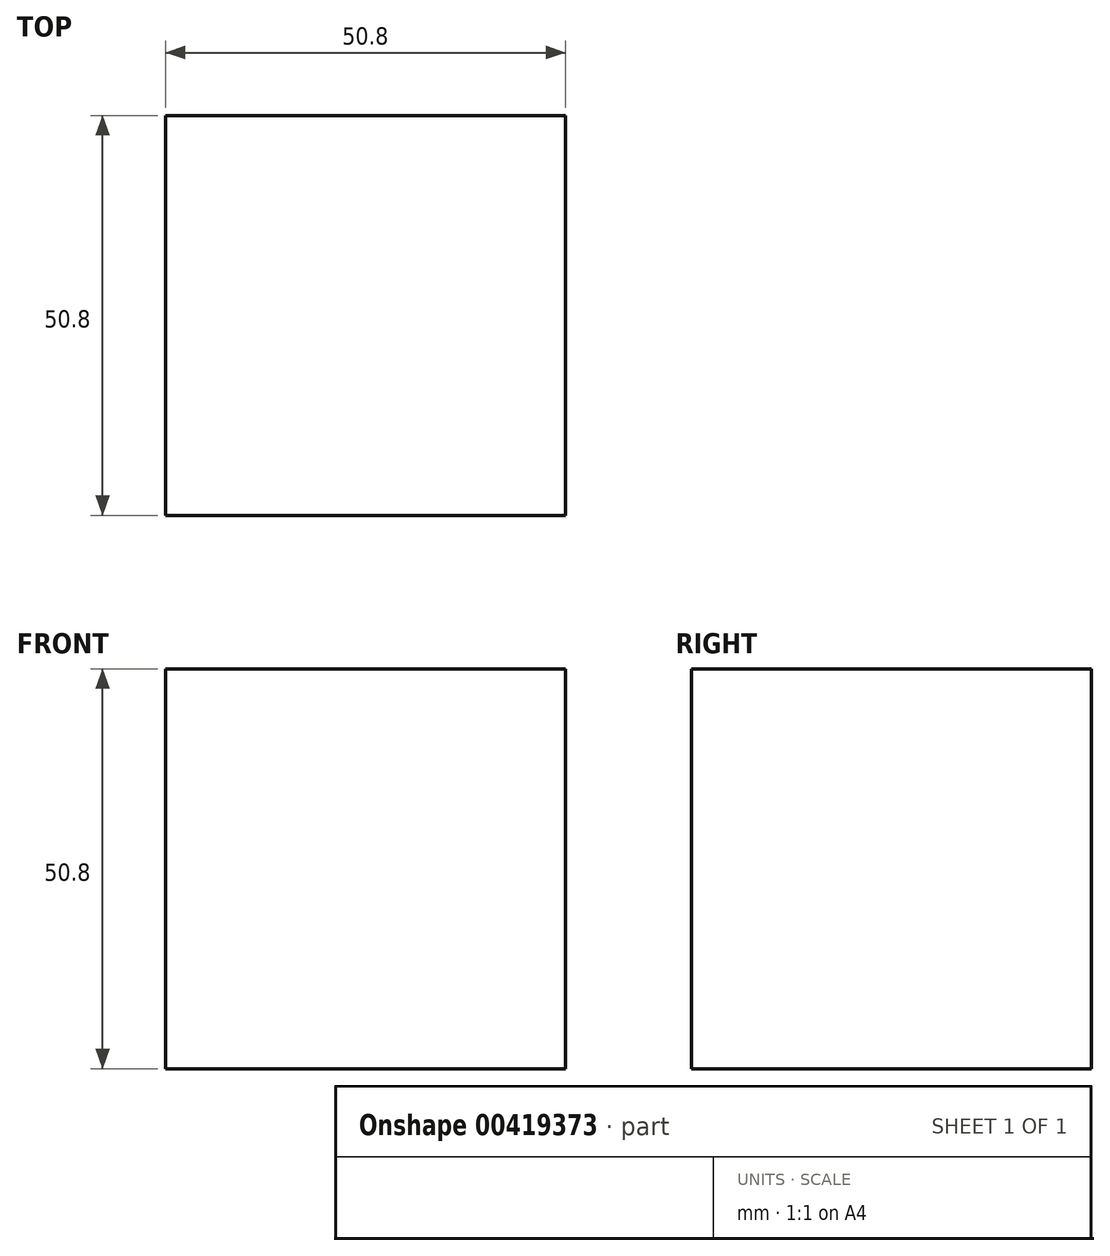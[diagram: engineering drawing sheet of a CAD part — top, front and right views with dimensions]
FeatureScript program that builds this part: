
annotation { "Feature Type Name" : "Feature", "Feature Type Description" : "" }
export const myFeature = defineFeature(function(context is Context, id is Id, definition is map)
    precondition{}
    {
        {
            var Q0;
            Q0=qCreatedBy(makeId("Front.planeOp"),FACE);
            var sketch = newSketch(context, id + "F0", { "sketchPlane" : qUnion([Q0])});
            skLineSegment(sketch, "E0", {"start": v(26.55, 20.82) * mm, "end": v(-24.25, 20.82) * mm});
            skLineSegment(sketch, "E1", {"start": v(-24.25, 20.82) * mm, "end": v(-24.25, -29.98) * mm});
            skLineSegment(sketch, "E2", {"start": v(-24.25, -29.98) * mm, "end": v(26.55, -29.98) * mm});
            skLineSegment(sketch, "E3", {"start": v(26.55, -29.98) * mm, "end": v(26.55, 20.82) * mm});
            skSolve(sketch);
        }
        {
            var Q0;
            Q0 = qSketchRegion(id + "F0", true);
            extrude(context, id + "F1", {"entities" : qUnion([Q0]), "depth" : 50.8 * mm});
        }
    });
